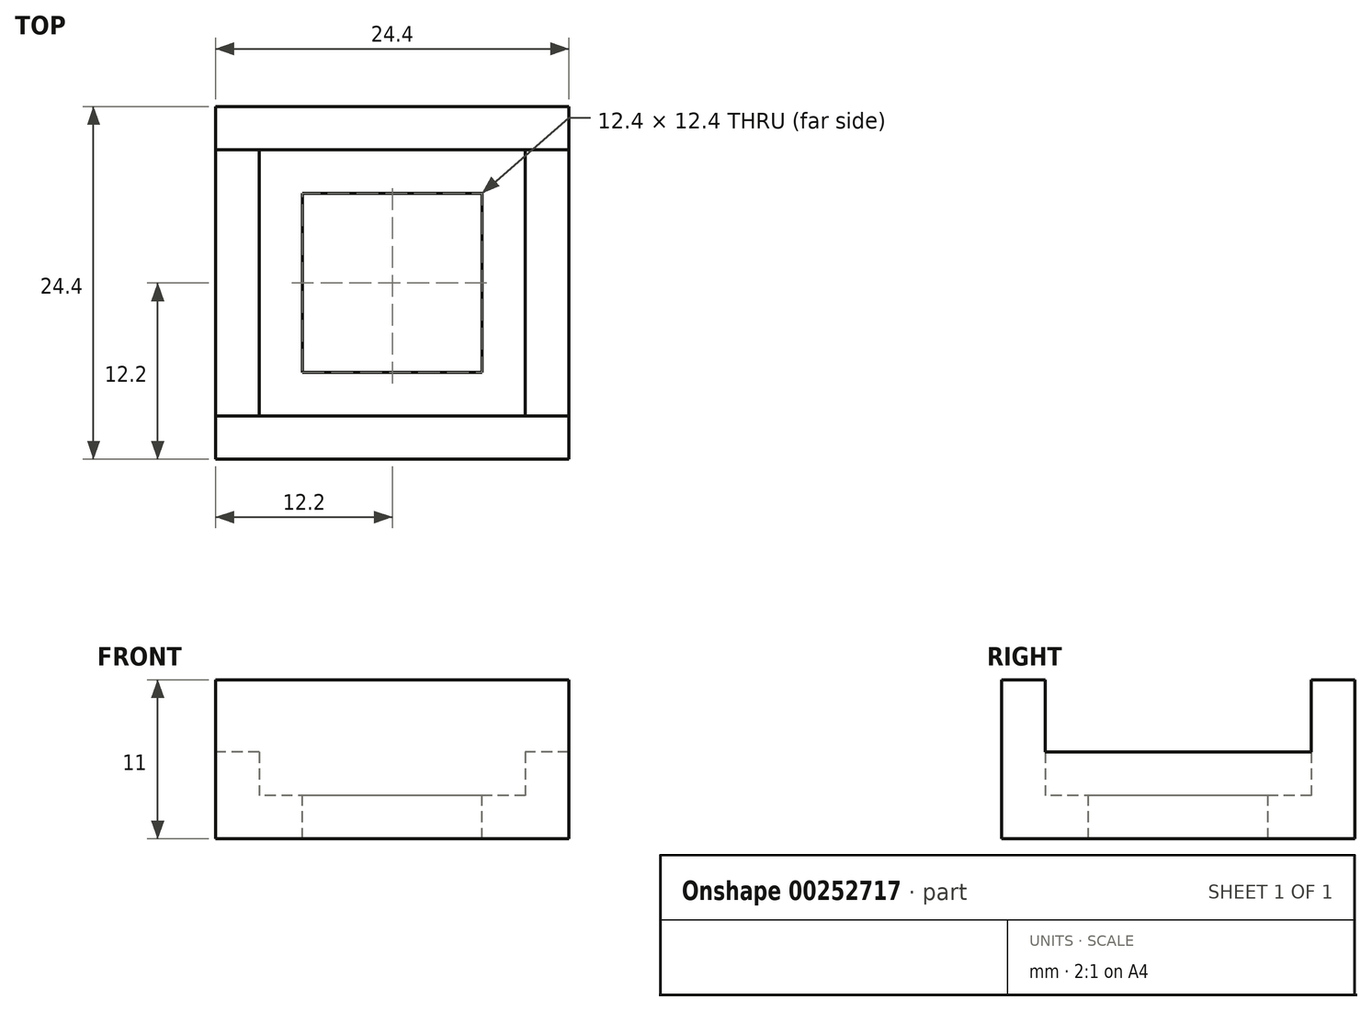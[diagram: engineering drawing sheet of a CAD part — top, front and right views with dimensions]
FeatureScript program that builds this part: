
annotation { "Feature Type Name" : "Feature", "Feature Type Description" : "" }
export const myFeature = defineFeature(function(context is Context, id is Id, definition is map)
    precondition{}
    {
        {
            var Q0;
            Q0=qCreatedBy(makeId("Top.planeOp"),FACE);
            var sketch = newSketch(context, id + "F0", { "sketchPlane" : qUnion([Q0])});
            skLineSegment(sketch, "E0.bottom", {"start": v(9.2, 9.2) * mm, "end": v(-9.2, 9.2) * mm});
            skLineSegment(sketch, "E0.top", {"start": v(9.2, -9.2) * mm, "end": v(-9.2, -9.2) * mm});
            skLineSegment(sketch, "E0.left", {"start": v(9.2, 9.2) * mm, "end": v(9.2, -9.2) * mm});
            skLineSegment(sketch, "E0.right", {"start": v(-9.2, 9.2) * mm, "end": v(-9.2, -9.2) * mm});
            skPoint(sketch, "E0.middle", {"position": v(0, 0) * mm});
            skLineSegment(sketch, "E1.0", {"start": v(12.2, 12.2) * mm, "end": v(-12.2, 12.2) * mm});
            skLineSegment(sketch, "E1.1", {"start": v(12.2, 12.2) * mm, "end": v(12.2, -12.2) * mm});
            skLineSegment(sketch, "E1.2", {"start": v(12.2, -12.2) * mm, "end": v(-12.2, -12.2) * mm});
            skLineSegment(sketch, "E1.3", {"start": v(-12.2, 12.2) * mm, "end": v(-12.2, -12.2) * mm});
            skSolve(sketch);
        }
        {
            var Q0;
            Q0 = qSketchRegion(id + "F0", true);
            extrude(context, id + "F1", {"entities" : qUnion([Q0]), "depth" : 3 * mm});
        }
        {
            var Q0;
            Q0=makeQuery(id+"F1.opExtrude","CAP_FACE",FACE,{"disambiguationData":[OSD([sQuery(id+"F0.wireOp",EDGE,"E0.bottom"),sQuery(id+"F0.wireOp",EDGE,"E0.top"),sQuery(id+"F0.wireOp",EDGE,"E0.left"),sQuery(id+"F0.wireOp",EDGE,"E0.right"),sQuery(id+"F0.wireOp",EDGE,"E1.0"),sQuery(id+"F0.wireOp",EDGE,"E1.1"),sQuery(id+"F0.wireOp",EDGE,"E1.2"),sQuery(id+"F0.wireOp",EDGE,"E1.3")])],"isStart":true});
            var sketch = newSketch(context, id + "F2", { "sketchPlane" : qUnion([Q0])});
            skLineSegment(sketch, "E2.0", {"start": v(12.2, 12.2) * mm, "end": v(-12.2, 12.2) * mm});
            skLineSegment(sketch, "E2.1", {"start": v(-12.2, -12.2) * mm, "end": v(-12.2, 12.2) * mm});
            skLineSegment(sketch, "E2.2", {"start": v(12.2, -12.2) * mm, "end": v(-12.2, -12.2) * mm});
            skLineSegment(sketch, "E2.3", {"start": v(12.2, -12.2) * mm, "end": v(12.2, 12.2) * mm});
            skLineSegment(sketch, "E3.0", {"start": v(6.2, 6.2) * mm, "end": v(-6.2, 6.2) * mm});
            skLineSegment(sketch, "E3.1", {"start": v(6.2, -6.2) * mm, "end": v(6.2, 6.2) * mm});
            skLineSegment(sketch, "E3.2", {"start": v(6.2, -6.2) * mm, "end": v(-6.2, -6.2) * mm});
            skLineSegment(sketch, "E3.3", {"start": v(-6.2, -6.2) * mm, "end": v(-6.2, 6.2) * mm});
            skSolve(sketch);
        }
        {
            var Q0;
            Q0 = qSketchRegion(id + "F2", true);
            extrude(context, id + "F3", {"entities" : qUnion([Q0]), "operationType" : NewBodyOperationType.ADD, "depth" : 3 * mm});
        }
        {
            var Q0;
            Q0=makeQuery(id+"F1.opExtrude","CAP_FACE",FACE,{"disambiguationData":[OSD([sQuery(id+"F0.wireOp",EDGE,"E0.bottom"),sQuery(id+"F0.wireOp",EDGE,"E0.top"),sQuery(id+"F0.wireOp",EDGE,"E0.left"),sQuery(id+"F0.wireOp",EDGE,"E0.right"),sQuery(id+"F0.wireOp",EDGE,"E1.0"),sQuery(id+"F0.wireOp",EDGE,"E1.1"),sQuery(id+"F0.wireOp",EDGE,"E1.2"),sQuery(id+"F0.wireOp",EDGE,"E1.3")])],"isStart":false});
            var sketch = newSketch(context, id + "F4", { "sketchPlane" : qUnion([Q0])});
            skLineSegment(sketch, "E4.bottom", {"start": v(-12.2, -12.2) * mm, "end": v(12.2, -12.2) * mm});
            skLineSegment(sketch, "E4.top", {"start": v(-12.2, -9.2) * mm, "end": v(12.2, -9.2) * mm});
            skLineSegment(sketch, "E4.left", {"start": v(-12.2, -12.2) * mm, "end": v(-12.2, -9.2) * mm});
            skLineSegment(sketch, "E4.right", {"start": v(12.2, -12.2) * mm, "end": v(12.2, -9.2) * mm});
            skLineSegment(sketch, "E5.bottom", {"start": v(-12.2, 12.2) * mm, "end": v(12.2, 12.2) * mm});
            skLineSegment(sketch, "E5.top", {"start": v(-12.2, 9.2) * mm, "end": v(12.2, 9.2) * mm});
            skLineSegment(sketch, "E5.left", {"start": v(-12.2, 12.2) * mm, "end": v(-12.2, 9.2) * mm});
            skLineSegment(sketch, "E5.right", {"start": v(12.2, 12.2) * mm, "end": v(12.2, 9.2) * mm});
            skSolve(sketch);
        }
        {
            var Q0;
            Q0 = qSketchRegion(id + "F4", true);
            extrude(context, id + "F5", {"entities" : qUnion([Q0]), "operationType" : NewBodyOperationType.ADD, "depth" : 5 * mm});
        }
    });
